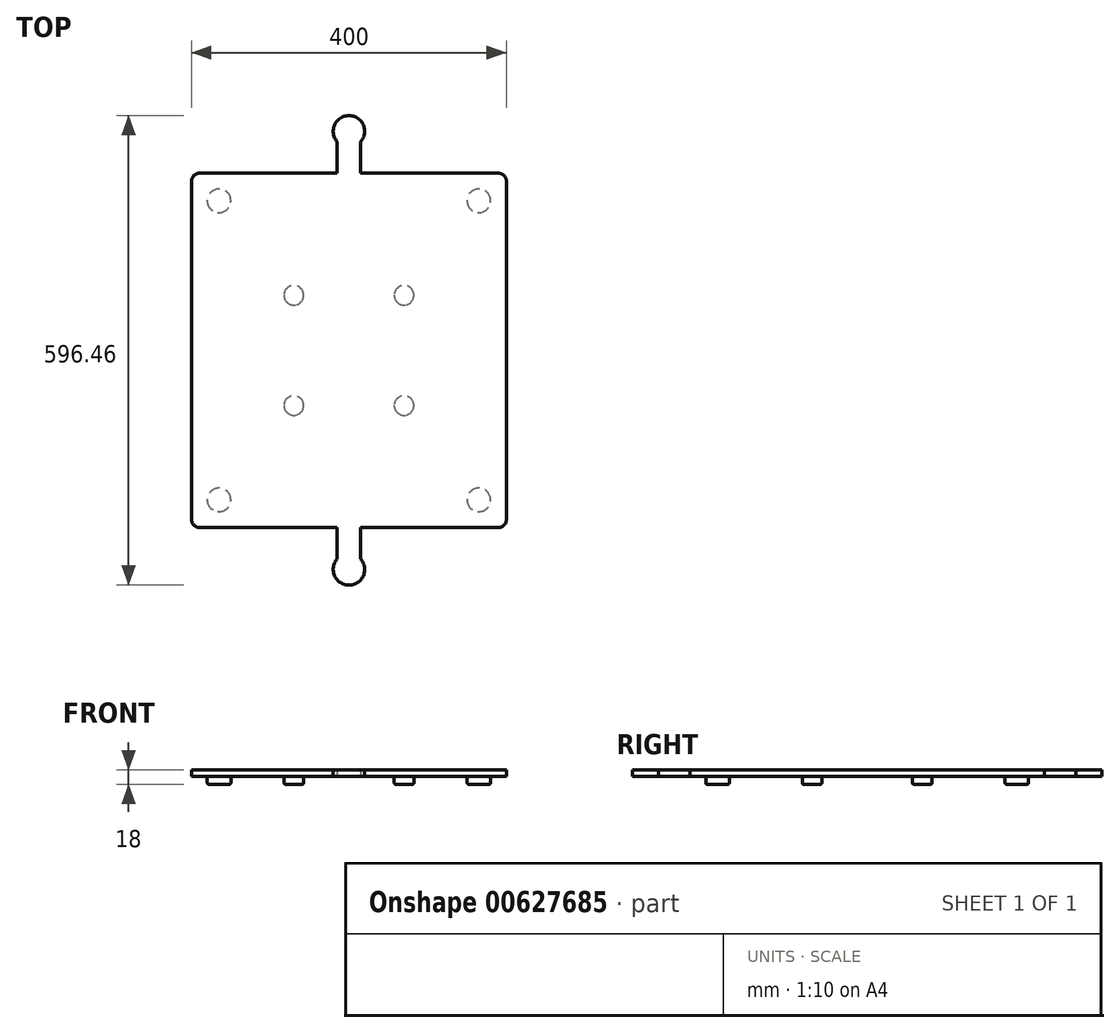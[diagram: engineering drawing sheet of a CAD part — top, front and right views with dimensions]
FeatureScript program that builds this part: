
annotation { "Feature Type Name" : "Feature", "Feature Type Description" : "" }
export const myFeature = defineFeature(function(context is Context, id is Id, definition is map)
    precondition{}
    {
        {
            var Q0;
            Q0=qCreatedBy(makeId("Top.planeOp"),FACE);
            var sketch = newSketch(context, id + "F0", { "sketchPlane" : qUnion([Q0])});
            skLineSegment(sketch, "E0", {"start": v(-200, 0) * mm, "end": v(-200, 215) * mm});
            skLineSegment(sketch, "E1", {"start": v(-190, 225) * mm, "end": v(0, 225) * mm});
            skPoint(sketch, "E2.visualSharp", {"position": v(-200, 225) * mm});
            skArc(sketch, "E2.filletArc", {"start": v(-190, 225) * mm, "mid": v(-197.07, 222.07) * mm, "end": v(-200, 215) * mm});
            skLineSegment(sketch, "E3.MirrorCS", {"start": v(200, 0) * mm, "end": v(200, 215) * mm});
            skLineSegment(sketch, "E4.MirrorCS", {"start": v(190, 225) * mm, "end": v(0, 225) * mm});
            skArc(sketch, "E5.MirrorCS", {"start": v(190, 225) * mm, "mid": v(197.07, 222.07) * mm, "end": v(200, 215) * mm});
            skArc(sketch, "E6.MirrorCS", {"start": v(-190, -225) * mm, "mid": v(-197.07, -222.07) * mm, "end": v(-200, -215) * mm});
            skPoint(sketch, "E7.MirrorP", {"position": v(-200, -225) * mm});
            skLineSegment(sketch, "E8.MirrorCS", {"start": v(200, 0) * mm, "end": v(200, -215) * mm});
            skLineSegment(sketch, "E9.MirrorCS", {"start": v(190, -225) * mm, "end": v(0, -225) * mm});
            skLineSegment(sketch, "E10.MirrorCS", {"start": v(-200, 0) * mm, "end": v(-200, -215) * mm});
            skArc(sketch, "E11.MirrorCS", {"start": v(190, -225) * mm, "mid": v(197.07, -222.07) * mm, "end": v(200, -215) * mm});
            skLineSegment(sketch, "E12.MirrorCS", {"start": v(-190, -225) * mm, "end": v(0, -225) * mm});
            skLineSegment(sketch, "E13.bottom", {"start": v(15, 225) * mm, "end": v(-15, 225) * mm});
            skLineSegment(sketch, "E13.top", {"start": v(15, 265) * mm, "end": v(-15, 265) * mm});
            skLineSegment(sketch, "E13.left", {"start": v(15, 225) * mm, "end": v(15, 265) * mm});
            skLineSegment(sketch, "E13.right", {"start": v(-15, 225) * mm, "end": v(-15, 265) * mm});
            skArc(sketch, "E14", {"start": v(15, 265) * mm, "mid": v(0, 298.23) * mm, "end": v(-15, 265) * mm});
            skLineSegment(sketch, "E15.MirrorCS", {"start": v(15, -265) * mm, "end": v(-15, -265) * mm});
            skLineSegment(sketch, "E16.MirrorCS", {"start": v(15, -225) * mm, "end": v(15, -265) * mm});
            skLineSegment(sketch, "E17.MirrorCS", {"start": v(-15, -225) * mm, "end": v(-15, -265) * mm});
            skArc(sketch, "E18.MirrorCS", {"start": v(15, -265) * mm, "mid": v(0, -298.23) * mm, "end": v(-15, -265) * mm});
            skSolve(sketch);
        }
        {
            var Q0;
            Q0 = qSketchRegion(id + "F0", true);
            extrude(context, id + "F1", {"entities" : qUnion([Q0]), "depth" : 18 * mm, "offsetDistance" : 25 * mm});
        }
        {
            var Q0;
            Q0=makeQuery(id+"F1.opExtrude","CAP_FACE",FACE,{"disambiguationData":[OSD([sQuery(id+"F0.wireOp",EDGE,"E0"),sQuery(id+"F0.wireOp",EDGE,"E1"),sQuery(id+"F0.wireOp",EDGE,"E2.filletArc"),sQuery(id+"F0.wireOp",EDGE,"E3.MirrorCS"),sQuery(id+"F0.wireOp",EDGE,"E4.MirrorCS"),sQuery(id+"F0.wireOp",EDGE,"E5.MirrorCS"),sQuery(id+"F0.wireOp",EDGE,"E6.MirrorCS"),sQuery(id+"F0.wireOp",EDGE,"E8.MirrorCS"),sQuery(id+"F0.wireOp",EDGE,"E9.MirrorCS"),sQuery(id+"F0.wireOp",EDGE,"E10.MirrorCS"),sQuery(id+"F0.wireOp",EDGE,"E11.MirrorCS"),sQuery(id+"F0.wireOp",EDGE,"E12.MirrorCS"),sQuery(id+"F0.wireOp",EDGE,"E13.left"),sQuery(id+"F0.wireOp",EDGE,"E13.right"),sQuery(id+"F0.wireOp",EDGE,"E14"),sQuery(id+"F0.wireOp",EDGE,"E16.MirrorCS"),sQuery(id+"F0.wireOp",EDGE,"E17.MirrorCS"),sQuery(id+"F0.wireOp",EDGE,"E18.MirrorCS")])],"isStart":true});
            var sketch = newSketch(context, id + "F2", { "sketchPlane" : qUnion([Q0])});
            skLineSegment(sketch, "E19.bottom", {"start": v(-287.66, 310.58) * mm, "end": v(309.88, 310.58) * mm});
            skLineSegment(sketch, "E19.top", {"start": v(-287.66, -303.18) * mm, "end": v(309.88, -303.18) * mm});
            skLineSegment(sketch, "E19.left", {"start": v(-287.66, 310.58) * mm, "end": v(-287.66, -303.18) * mm});
            skLineSegment(sketch, "E19.right", {"start": v(309.88, 310.58) * mm, "end": v(309.88, -303.18) * mm});
            skCircle(sketch, "E20", {"center": v(-165, 190) * mm, "radius": 15 * mm});
            skCircle(sketch, "E21", {"center": v(-70, 70) * mm, "radius": 12.5 * mm});
            skCircle(sketch, "E22.MirrorC", {"center": v(70, 70) * mm, "radius": 12.5 * mm});
            skCircle(sketch, "E23.MirrorC", {"center": v(165, 190) * mm, "radius": 15 * mm});
            skCircle(sketch, "E24.MirrorC", {"center": v(-70, -70) * mm, "radius": 12.5 * mm});
            skCircle(sketch, "E25.MirrorC", {"center": v(-165, -190) * mm, "radius": 15 * mm});
            skCircle(sketch, "E26.MirrorC", {"center": v(70, -70) * mm, "radius": 12.5 * mm});
            skCircle(sketch, "E27.MirrorC", {"center": v(165, -190) * mm, "radius": 15 * mm});
            skSolve(sketch);
        }
        {
            var Q0;
            Q0 = qSketchRegion(id + "F2", true);
            extrude(context, id + "F3", {"entities" : qUnion([Q0]), "operationType" : NewBodyOperationType.REMOVE, "oppositeDirection" : true, "depth" : 10 * mm, "offsetDistance" : 25 * mm});
        }
        {
            var Q0;
            Q0=makeQuery(id+"F3.boolean.opBoolean","COPY",FACE,{"derivedFrom":makeQuery(id+"F3.opExtrude","SWEPT_FACE",FACE,{"disambiguationData":[OSD([sQuery(id+"F2.wireOp",EDGE,"E27.MirrorC")])]})});
            var Q1;
            Q1=makeQuery(id+"F3.boolean.opBoolean","COPY",FACE,{"derivedFrom":makeQuery(id+"F3.opExtrude","SWEPT_FACE",FACE,{"disambiguationData":[OSD([sQuery(id+"F2.wireOp",EDGE,"E26.MirrorC")])]})});
            var Q2;
            Q2=makeQuery(id+"F3.boolean.opBoolean","COPY",FACE,{"derivedFrom":makeQuery(id+"F3.opExtrude","SWEPT_FACE",FACE,{"disambiguationData":[OSD([sQuery(id+"F2.wireOp",EDGE,"E22.MirrorC")])]})});
            var Q3;
            Q3=makeQuery(id+"F3.boolean.opBoolean","COPY",FACE,{"derivedFrom":makeQuery(id+"F3.opExtrude","SWEPT_FACE",FACE,{"disambiguationData":[OSD([sQuery(id+"F2.wireOp",EDGE,"E23.MirrorC")])]})});
            var Q4;
            Q4=makeQuery(id+"F3.boolean.opBoolean","COPY",FACE,{"derivedFrom":makeQuery(id+"F3.opExtrude","SWEPT_FACE",FACE,{"disambiguationData":[OSD([sQuery(id+"F2.wireOp",EDGE,"E21")])]})});
            var Q5;
            Q5=makeQuery(id+"F3.boolean.opBoolean","COPY",FACE,{"derivedFrom":makeQuery(id+"F3.opExtrude","SWEPT_FACE",FACE,{"disambiguationData":[OSD([sQuery(id+"F2.wireOp",EDGE,"E24.MirrorC")])]})});
            var Q6;
            Q6=makeQuery(id+"F3.boolean.opBoolean","COPY",FACE,{"derivedFrom":makeQuery(id+"F3.opExtrude","SWEPT_FACE",FACE,{"disambiguationData":[OSD([sQuery(id+"F2.wireOp",EDGE,"E20")])]})});
            var Q7;
            Q7=makeQuery(id+"F3.boolean.opBoolean","COPY",FACE,{"derivedFrom":makeQuery(id+"F3.opExtrude","SWEPT_FACE",FACE,{"disambiguationData":[OSD([sQuery(id+"F2.wireOp",EDGE,"E25.MirrorC")])]})});
            fillet(context, id + "F4", {"entities" : qUnion([Q0, Q1, Q2, Q3, Q4, Q5, Q6, Q7]), "radius" : 2 * mm, "tangentPropagation" : true, "allowEdgeOverflow" : false});
        }
    });
